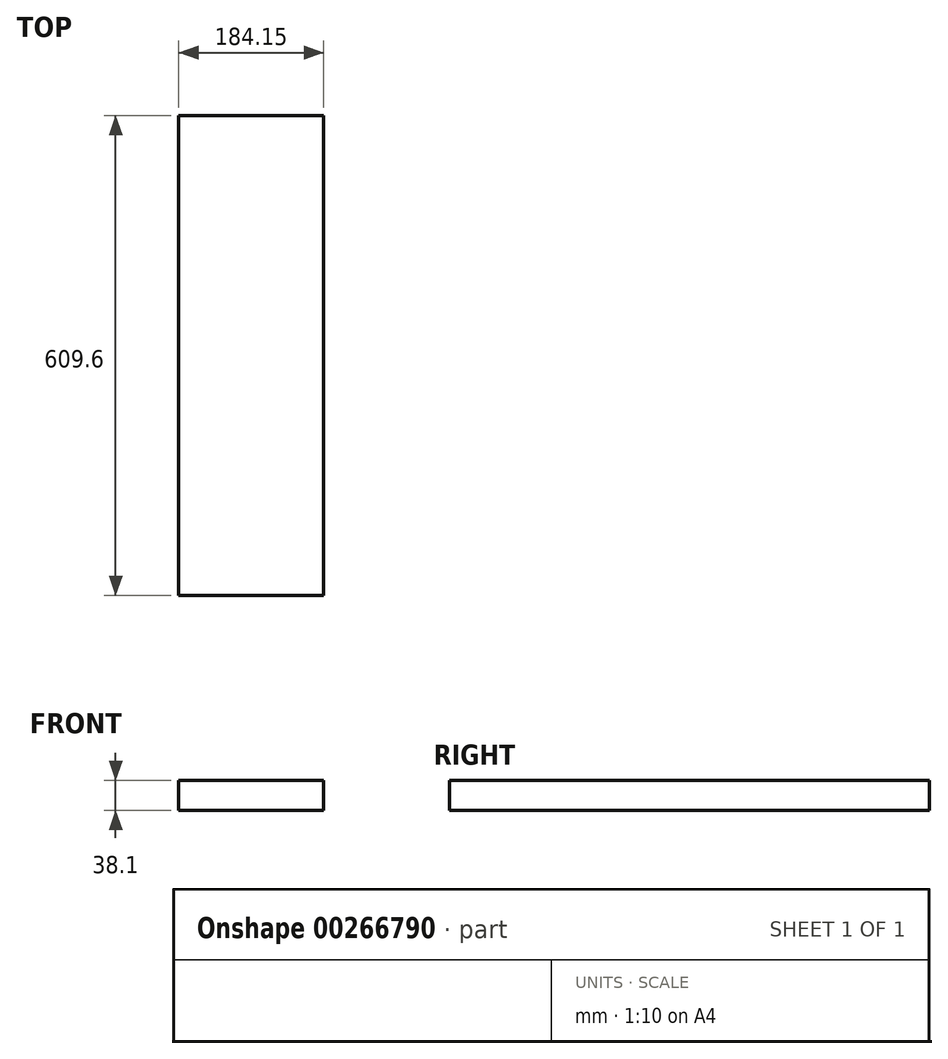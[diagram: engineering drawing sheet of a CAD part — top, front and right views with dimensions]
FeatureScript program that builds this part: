
annotation { "Feature Type Name" : "Feature", "Feature Type Description" : "" }
export const myFeature = defineFeature(function(context is Context, id is Id, definition is map)
    precondition{}
    {
        {
            var Q0;
            Q0=qCreatedBy(makeId("Front.planeOp"),FACE);
            var sketch = newSketch(context, id + "F0", { "sketchPlane" : qUnion([Q0])});
            skLineSegment(sketch, "E0.bottom", {"start": v(-48.34, 23.68) * mm, "end": v(135.8, 23.68) * mm});
            skLineSegment(sketch, "E0.top", {"start": v(-48.34, -14.42) * mm, "end": v(135.8, -14.42) * mm});
            skLineSegment(sketch, "E0.left", {"start": v(-48.34, 23.68) * mm, "end": v(-48.34, -14.42) * mm});
            skLineSegment(sketch, "E0.right", {"start": v(135.8, 23.68) * mm, "end": v(135.8, -14.42) * mm});
            skSolve(sketch);
        }
        {
            var Q0;
            Q0=qSketchRegion(id+"F0",true);
            extrude(context, id + "F1", {"entities" : qUnion([Q0]), "depth" : 609.6 * mm});
        }
    });
